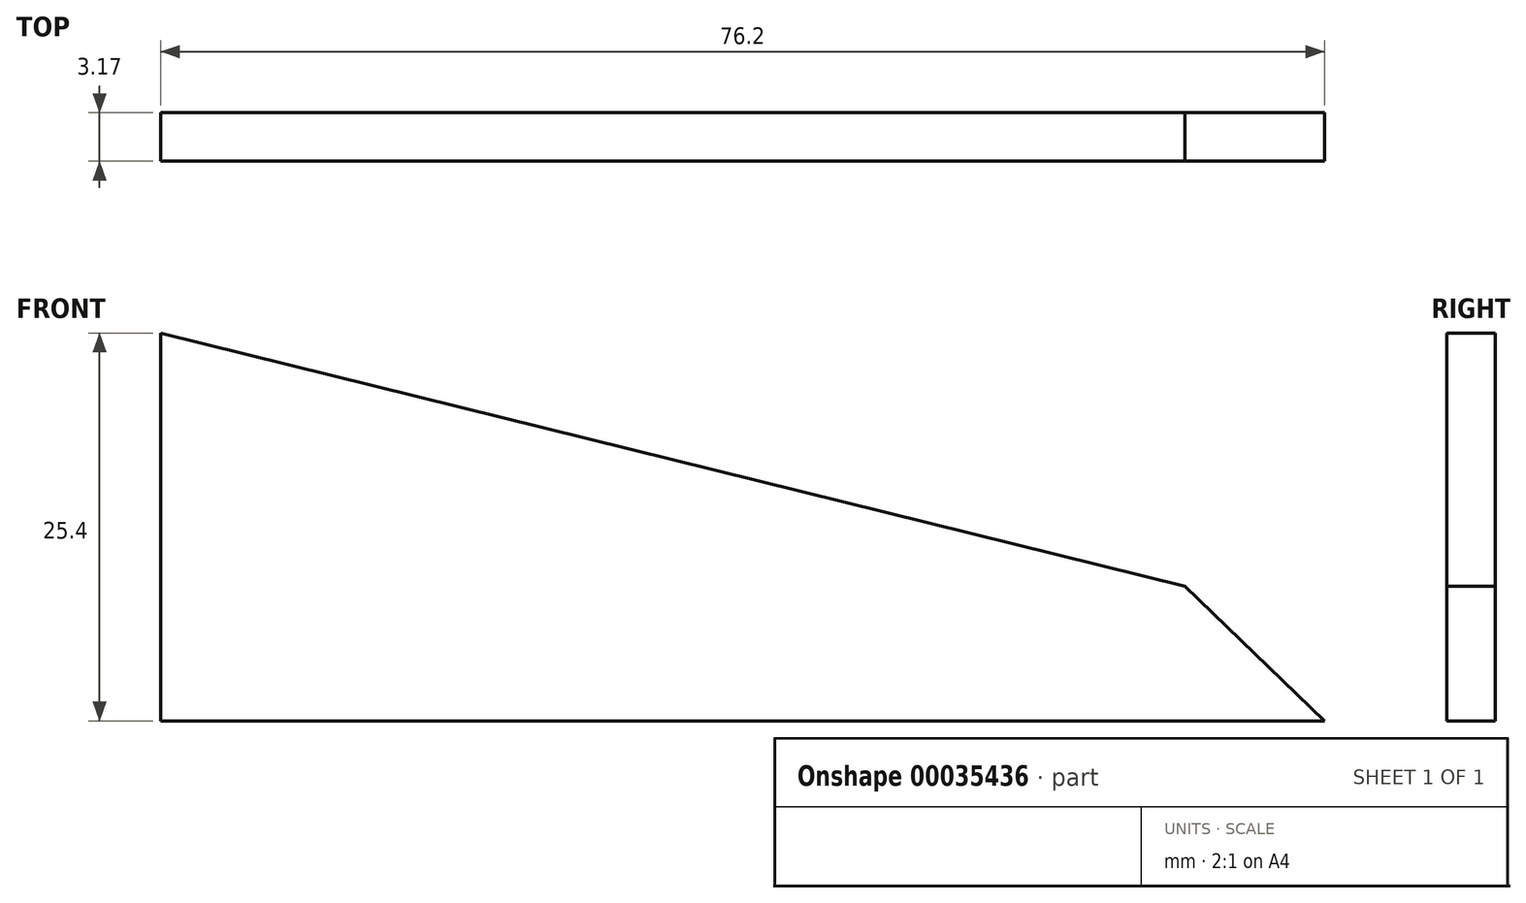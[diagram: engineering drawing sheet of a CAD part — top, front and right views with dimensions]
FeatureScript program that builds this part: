
annotation { "Feature Type Name" : "Feature", "Feature Type Description" : "" }
export const myFeature = defineFeature(function(context is Context, id is Id, definition is map)
    precondition{}
    {
        {
            var Q0;
            Q0=qCreatedBy(makeId("Front.planeOp"),FACE);
            var sketch = newSketch(context, id + "F0", { "sketchPlane" : qUnion([Q0])});
            skLineSegment(sketch, "E0", {"start": v(-42.79, 40.73) * mm, "end": v(33.41, 40.73) * mm});
            skLineSegment(sketch, "E1", {"start": v(-42.79, 40.73) * mm, "end": v(-42.79, 66.13) * mm});
            skLineSegment(sketch, "E2", {"start": v(-42.79, 66.13) * mm, "end": v(24.26, 49.53) * mm});
            skLineSegment(sketch, "E3", {"start": v(24.26, 49.53) * mm, "end": v(33.41, 40.73) * mm});
            skSolve(sketch);
        }
        {
            var Q0;
            Q0=makeQuery(id+"F0.imprint","IMPRINT",FACE,{"disambiguationData":[TD([[makeQuery(id+"F0.imprint","IMPRINT",EDGE,{"derivedFrom":sQuery(id+"F0.wireOp",EDGE,"E0")}),1.0]])]});
            extrude(context, id + "F1", {"entities" : qUnion([Q0]), "depth" : 3.17 * mm});
        }
    });
